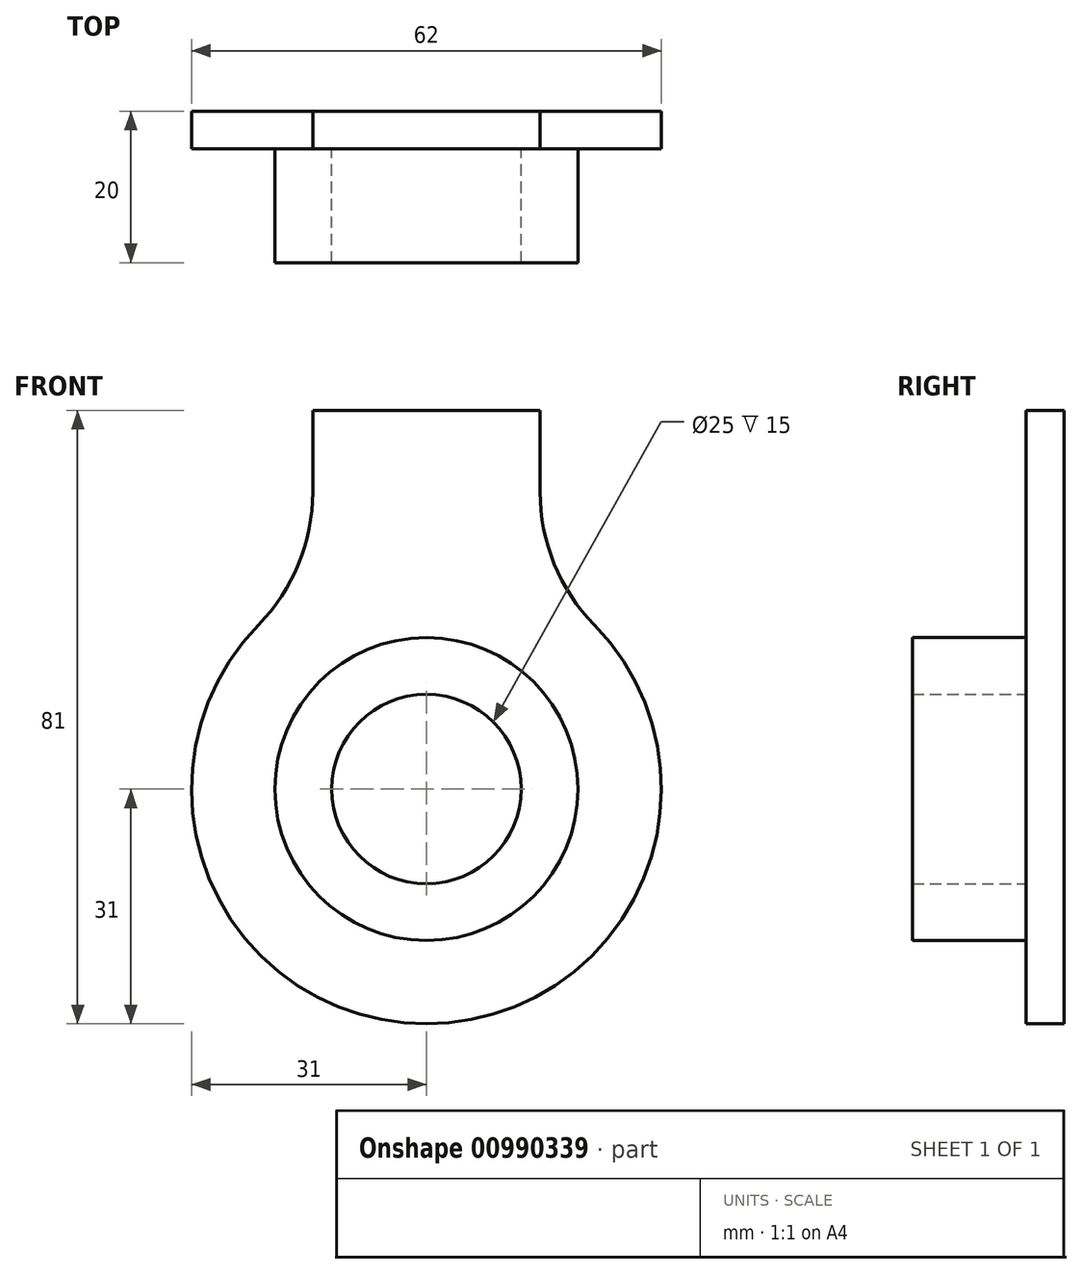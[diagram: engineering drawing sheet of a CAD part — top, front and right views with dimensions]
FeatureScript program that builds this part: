
annotation { "Feature Type Name" : "Feature", "Feature Type Description" : "" }
export const myFeature = defineFeature(function(context is Context, id is Id, definition is map)
    precondition{}
    {
        {
            var Q0;
            Q0=qCreatedBy(makeId("Front.planeOp"),FACE);
            var sketch = newSketch(context, id + "F0", { "sketchPlane" : qUnion([Q0])});
            skCircle(sketch, "E0", {"center": v(0, 0) * mm, "radius": 31 * mm});
            skLineSegment(sketch, "E1.bottom", {"start": v(15, 50) * mm, "end": v(-15, 50) * mm});
            skLineSegment(sketch, "E2", {"start": v(0, 0) * mm, "end": v(15, 0) * mm});
            skLineSegment(sketch, "E3", {"start": v(0, 0) * mm, "end": v(-15, 0) * mm});
            skLineSegment(sketch, "E4", {"start": v(-15, 0) * mm, "end": v(-15, 50) * mm});
            skLineSegment(sketch, "E5", {"start": v(15, 50) * mm, "end": v(15, 0) * mm});
            skSolve(sketch);
        }
        {
            var Q0;
            {var subQ4=sQuery(id+"F0.wireOp",EDGE,"E2");Q0=makeQuery(id+"F0.imprint","IMPRINT",FACE,{"disambiguationData":[TD([[makeQuery(id+"F0.imprint","IMPRINT",EDGE,{"derivedFrom":subQ4}),1.0]])]});}
            var Q1;
            {var subQ4=sQuery(id+"F0.wireOp",EDGE,"E2");Q1=makeQuery(id+"F0.imprint","IMPRINT",FACE,{"disambiguationData":[TD([[makeQuery(id+"F0.imprint","IMPRINT",EDGE,{"derivedFrom":subQ4}),-1.0]])]});}
            var Q2;
            {var subQ5=sQuery(id+"F0.wireOp",EDGE,"E1.bottom");Q2=makeQuery(id+"F0.imprint","IMPRINT",FACE,{"disambiguationData":[TD([[makeQuery(id+"F0.imprint","IMPRINT",EDGE,{"derivedFrom":subQ5}),1.0]])]});}
            extrude(context, id + "F1", {"entities" : qUnion([Q0, Q1, Q2]), "depth" : 5 * mm, "offsetDistance" : 25 * mm});
        }
        {
            var Q0;
            Q0=makeQuery(id+"F1.opExtrude","SWEPT_EDGE",EDGE,{"disambiguationData":[OSD([sQuery(id+"F0.wireOp",EDGE,"E0"),sQuery(id+"F0.wireOp",EDGE,"E4")])]});
            var Q1;
            Q1=makeQuery(id+"F1.opExtrude","SWEPT_EDGE",EDGE,{"disambiguationData":[OSD([sQuery(id+"F0.wireOp",EDGE,"E0"),sQuery(id+"F0.wireOp",EDGE,"E5")])]});
            fillet(context, id + "F2", {"entities" : qUnion([Q0, Q1]), "radius" : 25 * mm, "tangentPropagation" : true, "allowEdgeOverflow" : false});
        }
        {
            var Q0;
            Q0=makeQuery(id+"F1.opExtrude","CAP_FACE",FACE,{"disambiguationData":[OSD([sQuery(id+"F0.wireOp",EDGE,"E0"),sQuery(id+"F0.wireOp",EDGE,"E4"),sQuery(id+"F0.wireOp",EDGE,"E1.bottom"),sQuery(id+"F0.wireOp",EDGE,"E5")])],"isStart":false});
            var sketch = newSketch(context, id + "F3", { "sketchPlane" : qUnion([Q0])});
            skCircle(sketch, "E6", {"center": v(0, 0) * mm, "radius": 20 * mm});
            skCircle(sketch, "E7", {"center": v(0, 0) * mm, "radius": 12.5 * mm});
            skSolve(sketch);
        }
        {
            var Q0;
            Q0=makeQuery(id+"F3.imprint","IMPRINT",FACE,{"disambiguationData":[TD([[makeQuery(id+"F3.imprint","IMPRINT",EDGE,{"derivedFrom":sQuery(id+"F3.wireOp",EDGE,"E6")}),1.0]])]});
            extrude(context, id + "F4", {"entities" : qUnion([Q0]), "operationType" : NewBodyOperationType.ADD, "depth" : 15 * mm, "offsetDistance" : 25 * mm});
        }
    });
